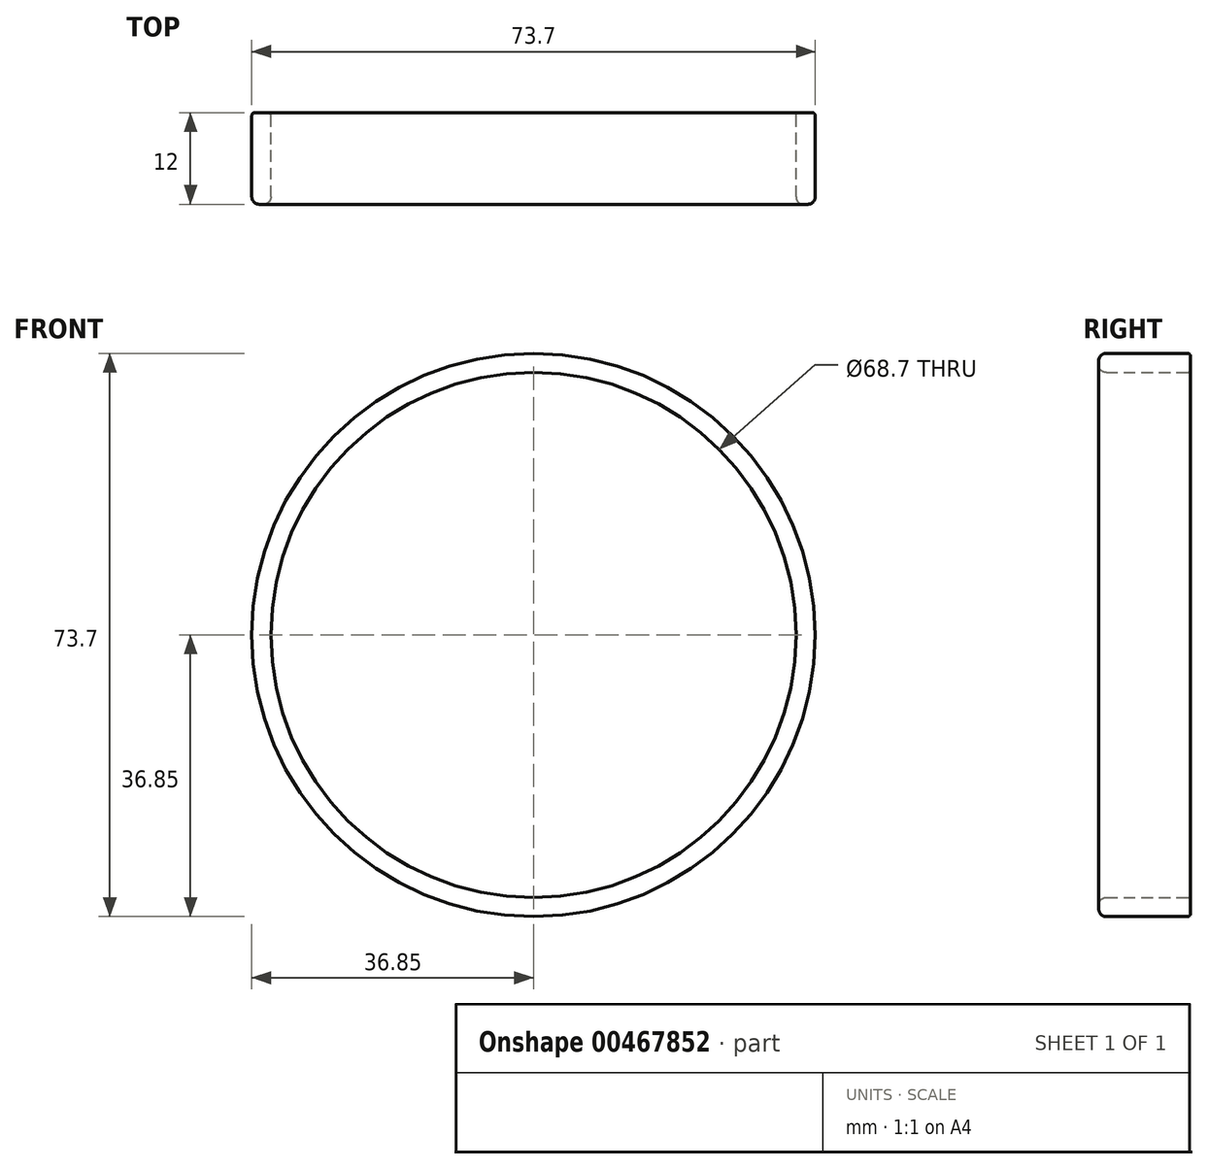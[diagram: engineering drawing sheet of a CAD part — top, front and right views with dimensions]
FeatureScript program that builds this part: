
annotation { "Feature Type Name" : "Feature", "Feature Type Description" : "" }
export const myFeature = defineFeature(function(context is Context, id is Id, definition is map)
    precondition{}
    {
        {
            var Q0;
            Q0=qCreatedBy(makeId("Front.planeOp"),FACE);
            var sketch = newSketch(context, id + "F0", { "sketchPlane" : qUnion([Q0])});
            skCircle(sketch, "E0", {"center": v(0, 0) * mm, "radius": 36.85 * mm});
            skCircle(sketch, "E1", {"center": v(0, 0) * mm, "radius": 34.35 * mm});
            skSolve(sketch);
        }
        {
            var Q0;
            Q0 = qSketchRegion(id + "F0", true);
            extrude(context, id + "F1", {"entities" : qUnion([Q0]), "depth" : 12 * mm});
        }
        {
            var Q0;
            Q0=makeQuery(id+"F1.opExtrude","CAP_EDGE",EDGE,{"disambiguationData":[OSD([sQuery(id+"F0.wireOp",EDGE,"E1")])],"isStart":false});
            var Q1;
            Q1=makeQuery(id+"F1.opExtrude","CAP_FACE",FACE,{"disambiguationData":[OSD([sQuery(id+"F0.wireOp",EDGE,"E0"),sQuery(id+"F0.wireOp",EDGE,"E1")])],"isStart":false});
            fillet(context, id + "F2", {"entities" : qUnion([Q0, Q1]), "radius" : 0.97 * mm, "tangentPropagation" : true, "allowEdgeOverflow" : false});
        }
        {
            var Q0;
            Q0=makeQuery(id+"F1.opExtrude","CAP_EDGE",EDGE,{"disambiguationData":[OSD([sQuery(id+"F0.wireOp",EDGE,"E1")])],"isStart":true});
            var Q1;
            Q1=makeQuery(id+"F1.opExtrude","CAP_EDGE",EDGE,{"disambiguationData":[OSD([sQuery(id+"F0.wireOp",EDGE,"E0")])],"isStart":true});
            fillet(context, id + "F3", {"entities" : qUnion([Q0, Q1]), "radius" : 0.4 * mm, "tangentPropagation" : true, "allowEdgeOverflow" : false});
        }
    });
